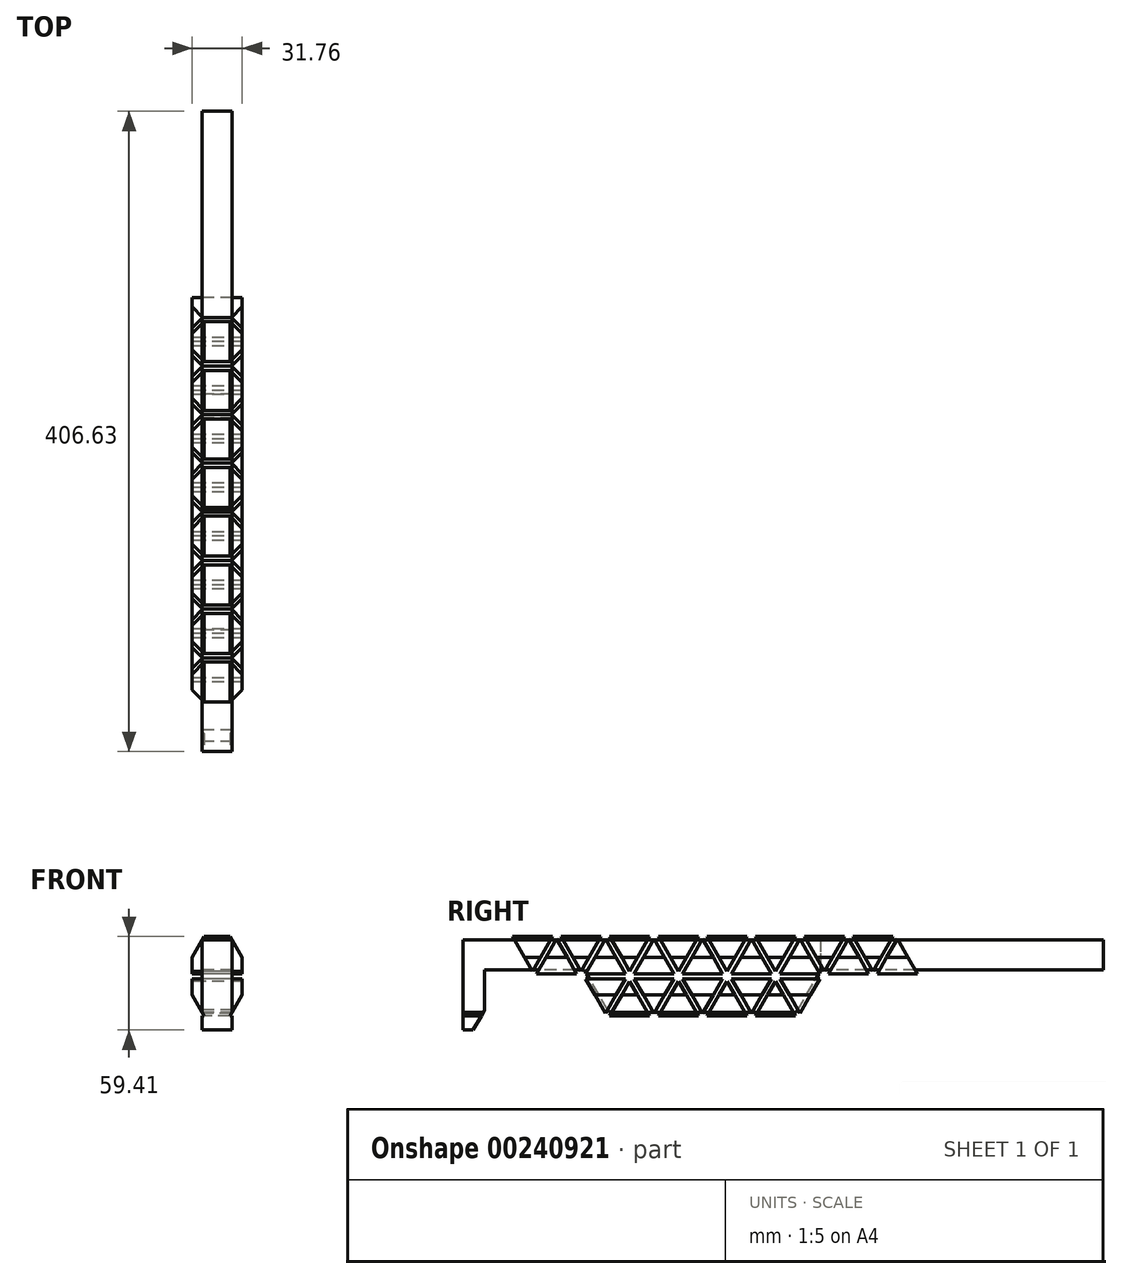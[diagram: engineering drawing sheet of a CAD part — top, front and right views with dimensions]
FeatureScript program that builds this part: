
annotation { "Feature Type Name" : "Feature", "Feature Type Description" : "" }
export const myFeature = defineFeature(function(context is Context, id is Id, definition is map)
    precondition{}
    {
        {
            var Q0;
            Q0=qCreatedBy(makeId("Right.planeOp"),FACE);
            var sketch = newSketch(context, id + "F0", { "sketchPlane" : qUnion([Q0])});
            skLineSegment(sketch, "E0", {"start": v(0, 0) * mm, "end": v(12.7, 22) * mm});
            skLineSegment(sketch, "E1", {"start": v(0, 0) * mm, "end": v(25.4, 0) * mm});
            skLineSegment(sketch, "E2", {"start": v(25.4, 0) * mm, "end": v(12.7, 22) * mm});
            skLineSegment(sketch, "E3", {"start": v(25.4, 0) * mm, "end": v(28.15, 1.59) * mm});
            skLineSegment(sketch, "E4", {"start": v(28.15, 1.59) * mm, "end": v(15.45, 23.58) * mm});
            skLineSegment(sketch, "E5", {"start": v(15.45, 23.58) * mm, "end": v(40.85, 23.58) * mm});
            skLineSegment(sketch, "E6", {"start": v(40.85, 23.58) * mm, "end": v(28.15, 1.59) * mm});
            skLineSegment(sketch, "E7", {"start": v(0, 0) * mm, "end": v(0, -3.18) * mm});
            skLineSegment(sketch, "E8", {"start": v(0, -1.59) * mm, "end": v(3.07, -1.59) * mm});
            skLineSegment(sketch, "E9.MirrorCS", {"start": v(25.4, -3.18) * mm, "end": v(12.7, -25.17) * mm});
            skLineSegment(sketch, "E10.MirrorCS", {"start": v(0, -3.18) * mm, "end": v(25.4, -3.18) * mm});
            skLineSegment(sketch, "E11.MirrorCS", {"start": v(15.45, -26.76) * mm, "end": v(40.85, -26.76) * mm});
            skLineSegment(sketch, "E12.MirrorCS", {"start": v(0, -3.17) * mm, "end": v(12.7, -25.17) * mm});
            skLineSegment(sketch, "E13.MirrorCS", {"start": v(40.85, -26.76) * mm, "end": v(28.15, -4.76) * mm});
            skLineSegment(sketch, "E14.MirrorCS", {"start": v(25.4, -3.17) * mm, "end": v(28.15, -4.76) * mm});
            skLineSegment(sketch, "E15.MirrorCS", {"start": v(28.15, -4.76) * mm, "end": v(15.45, -26.76) * mm});
            skLineSegment(sketch, "E16", {"start": v(28.15, 1.59) * mm, "end": v(28.15, -1.94) * mm});
            skLineSegment(sketch, "E17.MirrorCS", {"start": v(30.9, 0) * mm, "end": v(43.6, 22) * mm});
            skLineSegment(sketch, "E18.MirrorCS", {"start": v(56.3, 0) * mm, "end": v(30.9, 0) * mm});
            skLineSegment(sketch, "E19.MirrorCS", {"start": v(56.3, 0) * mm, "end": v(43.6, 22) * mm});
            skLineSegment(sketch, "E20.MirrorCS", {"start": v(30.9, -3.18) * mm, "end": v(43.6, -25.17) * mm});
            skLineSegment(sketch, "E21.MirrorCS", {"start": v(56.3, -3.18) * mm, "end": v(30.9, -3.18) * mm});
            skLineSegment(sketch, "E22.MirrorCS", {"start": v(56.3, -3.17) * mm, "end": v(43.6, -25.17) * mm});
            skLineSegment(sketch, "E23", {"start": v(43.6, 0) * mm, "end": v(43.6, 3.23) * mm});
            skLineSegment(sketch, "E24.MirrorCS", {"start": v(59.05, -4.76) * mm, "end": v(71.75, -26.76) * mm});
            skLineSegment(sketch, "E25.MirrorCS", {"start": v(59.05, 1.59) * mm, "end": v(71.75, 23.58) * mm});
            skLineSegment(sketch, "E26.MirrorCS", {"start": v(71.75, 23.58) * mm, "end": v(46.35, 23.58) * mm});
            skLineSegment(sketch, "E27.MirrorCS", {"start": v(46.35, 23.58) * mm, "end": v(59.05, 1.59) * mm});
            skLineSegment(sketch, "E28.MirrorCS", {"start": v(46.35, -26.76) * mm, "end": v(59.05, -4.76) * mm});
            skLineSegment(sketch, "E29.MirrorCS", {"start": v(71.75, -26.76) * mm, "end": v(46.35, -26.76) * mm});
            skLineSegment(sketch, "E30.1.0.0", {"start": v(87.2, 0) * mm, "end": v(74.5, 22) * mm});
            skLineSegment(sketch, "E30.1.0.1", {"start": v(87.2, 0) * mm, "end": v(61.8, 0) * mm});
            skLineSegment(sketch, "E30.1.0.2", {"start": v(61.8, 0) * mm, "end": v(74.5, 22) * mm});
            skLineSegment(sketch, "E30.1.0.3", {"start": v(77.25, 23.58) * mm, "end": v(89.95, 1.59) * mm});
            skLineSegment(sketch, "E30.1.0.4", {"start": v(102.65, 23.58) * mm, "end": v(77.25, 23.58) * mm});
            skLineSegment(sketch, "E30.1.0.5", {"start": v(89.95, 1.59) * mm, "end": v(102.65, 23.58) * mm});
            skLineSegment(sketch, "E30.2.0.0", {"start": v(118.1, 0) * mm, "end": v(105.4, 22) * mm});
            skLineSegment(sketch, "E30.2.0.1", {"start": v(118.1, 0) * mm, "end": v(92.7, 0) * mm});
            skLineSegment(sketch, "E30.2.0.2", {"start": v(92.7, 0) * mm, "end": v(105.4, 22) * mm});
            skLineSegment(sketch, "E30.2.0.3", {"start": v(108.15, 23.58) * mm, "end": v(120.85, 1.59) * mm});
            skLineSegment(sketch, "E30.2.0.4", {"start": v(133.55, 23.58) * mm, "end": v(108.15, 23.58) * mm});
            skLineSegment(sketch, "E30.2.0.5", {"start": v(120.85, 1.59) * mm, "end": v(133.55, 23.58) * mm});
            skLineSegment(sketch, "E30.direction1", {"start": v(56.3, 0) * mm, "end": v(87.2, 0) * mm, "construction": true});
            skLineSegment(sketch, "E31.1.0.0", {"start": v(149, 0) * mm, "end": v(136.3, 22) * mm});
            skLineSegment(sketch, "E31.1.0.1", {"start": v(123.6, 0) * mm, "end": v(136.3, 22) * mm});
            skLineSegment(sketch, "E31.1.0.2", {"start": v(149, 0) * mm, "end": v(123.6, 0) * mm});
            skLineSegment(sketch, "E31.direction1", {"start": v(118.1, 0) * mm, "end": v(149, 0) * mm, "construction": true});
            skLineSegment(sketch, "E32.MirrorCS", {"start": v(87.2, -3.17) * mm, "end": v(74.5, -25.17) * mm});
            skLineSegment(sketch, "E33.MirrorCS", {"start": v(61.8, -3.18) * mm, "end": v(74.5, -25.17) * mm});
            skLineSegment(sketch, "E34", {"start": v(87.2, -3.17) * mm, "end": v(61.8, -3.18) * mm});
            skLineSegment(sketch, "E35.1.0.0", {"start": v(-30.9, -3.18) * mm, "end": v(-5.5, -3.18) * mm});
            skLineSegment(sketch, "E35.1.0.1", {"start": v(-30.9, 0) * mm, "end": v(-5.5, 0) * mm});
            skLineSegment(sketch, "E35.1.0.2", {"start": v(-5.5, 0) * mm, "end": v(-18.2, 22) * mm});
            skLineSegment(sketch, "E35.1.0.3", {"start": v(-30.9, -3.17) * mm, "end": v(-18.2, -25.17) * mm});
            skLineSegment(sketch, "E35.1.0.4", {"start": v(-30.9, 0) * mm, "end": v(-18.2, 22) * mm});
            skLineSegment(sketch, "E35.1.0.5", {"start": v(-2.75, 1.59) * mm, "end": v(-15.45, 23.58) * mm});
            skLineSegment(sketch, "E35.1.0.6", {"start": v(-2.75, -4.76) * mm, "end": v(-15.45, -26.76) * mm});
            skLineSegment(sketch, "E35.1.0.7", {"start": v(-5.5, -3.18) * mm, "end": v(-18.2, -25.17) * mm});
            skLineSegment(sketch, "E35.1.0.8", {"start": v(9.95, -26.76) * mm, "end": v(-2.75, -4.76) * mm});
            skLineSegment(sketch, "E35.1.0.9", {"start": v(-15.45, -26.76) * mm, "end": v(9.95, -26.76) * mm});
            skLineSegment(sketch, "E35.1.0.10", {"start": v(9.95, 23.58) * mm, "end": v(-2.75, 1.59) * mm});
            skLineSegment(sketch, "E35.1.0.11", {"start": v(-15.45, 23.58) * mm, "end": v(9.95, 23.58) * mm});
            skLineSegment(sketch, "E35.2.0.0", {"start": v(-61.8, -3.18) * mm, "end": v(-36.4, -3.18) * mm});
            skLineSegment(sketch, "E35.2.0.1", {"start": v(-61.8, 0) * mm, "end": v(-36.4, 0) * mm});
            skLineSegment(sketch, "E35.2.0.2", {"start": v(-36.4, 0) * mm, "end": v(-49.1, 22) * mm});
            skLineSegment(sketch, "E35.2.0.3", {"start": v(-61.8, -3.17) * mm, "end": v(-49.1, -25.17) * mm});
            skLineSegment(sketch, "E35.2.0.4", {"start": v(-61.8, 0) * mm, "end": v(-49.1, 22) * mm});
            skLineSegment(sketch, "E35.2.0.5", {"start": v(-33.65, 1.59) * mm, "end": v(-46.35, 23.58) * mm});
            skLineSegment(sketch, "E35.2.0.6", {"start": v(-33.65, -4.76) * mm, "end": v(-46.35, -26.76) * mm});
            skLineSegment(sketch, "E35.2.0.7", {"start": v(-36.4, -3.18) * mm, "end": v(-49.1, -25.17) * mm});
            skLineSegment(sketch, "E35.2.0.8", {"start": v(-20.95, -26.76) * mm, "end": v(-33.65, -4.76) * mm});
            skLineSegment(sketch, "E35.2.0.9", {"start": v(-46.35, -26.76) * mm, "end": v(-20.95, -26.76) * mm});
            skLineSegment(sketch, "E35.2.0.10", {"start": v(-20.95, 23.58) * mm, "end": v(-33.65, 1.59) * mm});
            skLineSegment(sketch, "E35.2.0.11", {"start": v(-46.35, 23.58) * mm, "end": v(-20.95, 23.58) * mm});
            skLineSegment(sketch, "E35.direction1", {"start": v(12.7, -25.17) * mm, "end": v(-18.2, -25.17) * mm, "construction": true});
            skLineSegment(sketch, "E36.1.0.0", {"start": v(-64.55, 1.59) * mm, "end": v(-77.25, 23.58) * mm});
            skLineSegment(sketch, "E36.1.0.1", {"start": v(-51.85, 23.58) * mm, "end": v(-64.55, 1.59) * mm});
            skLineSegment(sketch, "E36.1.0.2", {"start": v(-77.25, 23.58) * mm, "end": v(-51.85, 23.58) * mm});
            skLineSegment(sketch, "E36.1.0.3", {"start": v(-67.3, 0) * mm, "end": v(-80, 22) * mm});
            skLineSegment(sketch, "E36.1.0.4", {"start": v(-92.7, 0) * mm, "end": v(-67.3, 0) * mm});
            skLineSegment(sketch, "E36.1.0.5", {"start": v(-92.7, 0) * mm, "end": v(-80, 22) * mm});
            skLineSegment(sketch, "E36.1.0.6", {"start": v(-82.75, 23.58) * mm, "end": v(-95.45, 1.59) * mm});
            skLineSegment(sketch, "E36.1.0.7", {"start": v(-108.15, 23.58) * mm, "end": v(-82.75, 23.58) * mm});
            skLineSegment(sketch, "E36.1.0.8", {"start": v(-95.45, 1.59) * mm, "end": v(-108.15, 23.58) * mm});
            skLineSegment(sketch, "E36.direction1", {"start": v(-2.75, 1.59) * mm, "end": v(-64.55, 1.59) * mm, "construction": true});
            skSolve(sketch);
        }
        {
            var Q0;
            Q0=qCreatedBy(makeId("Right.planeOp"),FACE);
            var sketch = newSketch(context, id + "F1", { "sketchPlane" : qUnion([Q0])});
            skLineSegment(sketch, "E37.0", {"start": v(-15.45, 23.58) * mm, "end": v(9.95, 23.58) * mm});
            skLineSegment(sketch, "E38.0", {"start": v(0, 0) * mm, "end": v(25.4, 0) * mm});
            skLineSegment(sketch, "E39", {"start": v(9.95, 23.58) * mm, "end": v(9.95, 0) * mm});
            skLineSegment(sketch, "E40", {"start": v(9.95, 11.8) * mm, "end": v(13.13, 11.8) * mm});
            skLineSegment(sketch, "E41", {"start": v(13.13, 11.8) * mm, "end": v(13.13, 21.32) * mm});
            skLineSegment(sketch, "E42", {"start": v(13.13, 11.8) * mm, "end": v(13.13, 2.27) * mm});
            skLineSegment(sketch, "E43", {"start": v(13.13, 21.32) * mm, "end": v(267.13, 21.32) * mm});
            skLineSegment(sketch, "E44", {"start": v(267.13, 21.32) * mm, "end": v(267.13, 2.27) * mm});
            skLineSegment(sketch, "E45", {"start": v(267.13, 2.27) * mm, "end": v(13.13, 2.27) * mm});
            skLineSegment(sketch, "E46", {"start": v(-15.45, 23.58) * mm, "end": v(-15.45, 29.93) * mm});
            skLineSegment(sketch, "E47", {"start": v(-15.45, 29.93) * mm, "end": v(9.95, 29.93) * mm});
            skLineSegment(sketch, "E48", {"start": v(9.95, 29.93) * mm, "end": v(9.95, 23.58) * mm});
            skLineSegment(sketch, "E49", {"start": v(9.95, 29.93) * mm, "end": v(-2.75, 51.93) * mm});
            skLineSegment(sketch, "E50", {"start": v(-2.75, 51.93) * mm, "end": v(-15.45, 29.93) * mm});
            skLineSegment(sketch, "E51", {"start": v(-15.45, 26.76) * mm, "end": v(-12.72, 26.76) * mm});
            skLineSegment(sketch, "E52.0", {"start": v(-5.5, 0) * mm, "end": v(-18.2, 22) * mm});
            skLineSegment(sketch, "E53.0", {"start": v(-30.9, 0) * mm, "end": v(-18.2, 22) * mm});
            skLineSegment(sketch, "E54.0", {"start": v(-30.9, 0) * mm, "end": v(-5.5, 0) * mm});
            skLineSegment(sketch, "E55.0", {"start": v(0, 0) * mm, "end": v(12.7, 22) * mm});
            skLineSegment(sketch, "E56.0", {"start": v(25.4, 0) * mm, "end": v(12.7, 22) * mm});
            skLineSegment(sketch, "E57.0.2", {"start": v(12.7, 22) * mm, "end": v(0, 0) * mm});
            skLineSegment(sketch, "E58.MirrorCS", {"start": v(-5.5, 53.52) * mm, "end": v(-18.2, 31.52) * mm});
            skLineSegment(sketch, "E59.MirrorCS", {"start": v(-30.9, 53.52) * mm, "end": v(-18.2, 31.52) * mm});
            skLineSegment(sketch, "E60.MirrorCS", {"start": v(-30.9, 53.52) * mm, "end": v(-5.5, 53.52) * mm});
            skLineSegment(sketch, "E61.MirrorCS", {"start": v(0, 53.52) * mm, "end": v(12.7, 31.52) * mm});
            skLineSegment(sketch, "E62.MirrorCS", {"start": v(25.4, 53.52) * mm, "end": v(12.7, 31.52) * mm});
            skLineSegment(sketch, "E63.MirrorCS", {"start": v(0, 53.52) * mm, "end": v(25.4, 53.52) * mm});
            skLineSegment(sketch, "E64.0", {"start": v(-36.4, -3.18) * mm, "end": v(-49.1, -25.17) * mm});
            skLineSegment(sketch, "E65", {"start": v(-42.75, -14.17) * mm, "end": v(-40, -15.76) * mm});
            skLineSegment(sketch, "E66", {"start": v(-41.37, -14.97) * mm, "end": v(-63.1, -74.64) * mm});
            skLineSegment(sketch, "E67", {"start": v(-63.1, -74.64) * mm, "end": v(-56.74, -85.64) * mm});
            skLineSegment(sketch, "E68", {"start": v(-63.1, -74.64) * mm, "end": v(-69.44, -63.64) * mm});
            skLineSegment(sketch, "E69", {"start": v(13.13, 21.32) * mm, "end": v(-139.5, 21.32) * mm});
            skLineSegment(sketch, "E70.0", {"start": v(-36.4, 0) * mm, "end": v(-49.1, 22) * mm});
            skLineSegment(sketch, "E71.0", {"start": v(-61.8, -3.17) * mm, "end": v(-49.1, -25.17) * mm});
            skPoint(sketch, "E72.0", {"position": v(12.7, -3.18) * mm});
            skLineSegment(sketch, "E73.0", {"start": v(46.35, -26.76) * mm, "end": v(59.05, -4.76) * mm});
            skLineSegment(sketch, "E74.0", {"start": v(87.2, -3.17) * mm, "end": v(74.5, -25.17) * mm});
            skLineSegment(sketch, "E75", {"start": v(72.27, -24.5) * mm, "end": v(-46.87, -24.5) * mm});
            skLineSegment(sketch, "E76", {"start": v(72.27, -24.5) * mm, "end": v(87.72, 2.27) * mm});
            skLineSegment(sketch, "E77", {"start": v(87.72, 2.27) * mm, "end": v(87.72, 21.32) * mm});
            skLineSegment(sketch, "E78", {"start": v(13.13, 2.27) * mm, "end": v(-125.82, 2.27) * mm});
            skLineSegment(sketch, "E79", {"start": v(-46.87, -24.5) * mm, "end": v(-62.32, 2.27) * mm});
            skLineSegment(sketch, "E80", {"start": v(-69.44, -63.64) * mm, "end": v(-51.98, -15.65) * mm});
            skLineSegment(sketch, "E81", {"start": v(-56.74, -85.64) * mm, "end": v(-34.49, -24.5) * mm});
            skLineSegment(sketch, "E82", {"start": v(-125.82, 2.27) * mm, "end": v(-125.82, -23.13) * mm});
            skLineSegment(sketch, "E83", {"start": v(-125.82, -23.13) * mm, "end": v(-133.15, -35.83) * mm});
            skLineSegment(sketch, "E84", {"start": v(-133.15, -35.83) * mm, "end": v(-139.5, -35.83) * mm});
            skLineSegment(sketch, "E85", {"start": v(-139.5, -35.83) * mm, "end": v(-139.5, 21.32) * mm});
            skSolve(sketch);
        }
        {
            var Q0;
            {var subQ0=sQuery(id+"F1.wireOp",EDGE,"E82");Q0=makeQuery(id+"F1.imprint","IMPRINT",FACE,{"disambiguationData":[TD([[makeQuery(id+"F1.imprint","IMPRINT",EDGE,{"derivedFrom":subQ0}),-1.0]])]});}
            var Q1;
            {var subQ0=sQuery(id+"F1.wireOp",EDGE,"E69");var subQ1=sQuery(id+"F1.wireOp",EDGE,"E53.0");var subQ2=makeQuery(id+"F1.imprint","INTERSECT",VERTEX,{"derivedFrom":[subQ1,subQ0]});Q1=makeQuery(id+"F1.imprint","IMPRINT",FACE,{"disambiguationData":[TD([[makeQuery(id+"F1.imprint","IMPRINT",EDGE,{"disambiguationData":[TD([[subQ2,1.0]])],"derivedFrom":subQ1}),1.0]])]});}
            var Q2;
            {var subQ0=sQuery(id+"F1.wireOp",EDGE,"E69");var subQ1=sQuery(id+"F1.wireOp",EDGE,"E52.0");var subQ2=makeQuery(id+"F1.imprint","INTERSECT",VERTEX,{"derivedFrom":[subQ1,subQ0]});Q2=makeQuery(id+"F1.imprint","IMPRINT",FACE,{"disambiguationData":[TD([[makeQuery(id+"F1.imprint","IMPRINT",EDGE,{"disambiguationData":[TD([[subQ2,1.0]])],"derivedFrom":subQ1}),1.0]])]});}
            var Q3;
            {var subQ0=sQuery(id+"F1.wireOp",EDGE,"E69");var subQ1=sQuery(id+"F1.wireOp",EDGE,"E39");var subQ2=makeQuery(id+"F1.imprint","INTERSECT",VERTEX,{"derivedFrom":[subQ1,subQ0]});Q3=makeQuery(id+"F1.imprint","IMPRINT",FACE,{"disambiguationData":[TD([[makeQuery(id+"F1.imprint","IMPRINT",EDGE,{"disambiguationData":[TD([[subQ2,-1.0]])],"derivedFrom":subQ1}),-1.0]])]});}
            var Q4;
            {var subQ0=sQuery(id+"F1.wireOp",EDGE,"E42");Q4=makeQuery(id+"F1.imprint","IMPRINT",FACE,{"disambiguationData":[TD([[makeQuery(id+"F1.imprint","IMPRINT",EDGE,{"derivedFrom":subQ0}),1.0]])]});}
            var Q5;
            {var subQ0=sQuery(id+"F1.wireOp",EDGE,"E40");Q5=makeQuery(id+"F1.imprint","IMPRINT",FACE,{"disambiguationData":[TD([[makeQuery(id+"F1.imprint","IMPRINT",EDGE,{"derivedFrom":subQ0}),-1.0]])]});}
            var Q6;
            {var subQ1=sQuery(id+"F1.wireOp",EDGE,"E40");Q6=makeQuery(id+"F1.imprint","IMPRINT",FACE,{"disambiguationData":[TD([[makeQuery(id+"F1.imprint","IMPRINT",EDGE,{"derivedFrom":subQ1}),1.0]])]});}
            var Q7;
            {var subQ0=sQuery(id+"F1.wireOp",EDGE,"E39");var subQ1=makeQuery(id+"F1.imprint","INTERSECT",VERTEX,{"derivedFrom":[subQ0,sQuery(id+"F1.wireOp",EDGE,"E40")]});Q7=makeQuery(id+"F1.imprint","IMPRINT",FACE,{"disambiguationData":[TD([[makeQuery(id+"F1.imprint","IMPRINT",EDGE,{"disambiguationData":[TD([[subQ1,1.0]])],"derivedFrom":subQ0}),-1.0]])]});}
            var Q8;
            {var subQ0=sQuery(id+"F1.wireOp",EDGE,"E69");var subQ1=sQuery(id+"F1.wireOp",EDGE,"E39");var subQ2=makeQuery(id+"F1.imprint","INTERSECT",VERTEX,{"derivedFrom":[subQ1,subQ0]});Q8=makeQuery(id+"F1.imprint","IMPRINT",FACE,{"disambiguationData":[TD([[makeQuery(id+"F1.imprint","IMPRINT",EDGE,{"disambiguationData":[TD([[subQ2,-1.0]])],"derivedFrom":subQ1}),1.0]])]});}
            var Q9;
            {var subQ7=sQuery(id+"F1.wireOp",EDGE,"E77");Q9=makeQuery(id+"F1.imprint","IMPRINT",FACE,{"disambiguationData":[TD([[makeQuery(id+"F1.imprint","IMPRINT",EDGE,{"derivedFrom":subQ7}),1.0]])]});}
            var Q10;
            {var subQ20=sQuery(id+"F1.wireOp",EDGE,"E54.0");Q10=makeQuery(id+"F1.imprint","IMPRINT",FACE,{"disambiguationData":[TD([[makeQuery(id+"F1.imprint","IMPRINT",EDGE,{"derivedFrom":subQ20}),-1.0]])]});}
            var Q11;
            {var subQ0=sQuery(id+"F1.wireOp",EDGE,"E38.0");var subQ1=sQuery(id+"F1.wireOp",EDGE,"E39");var subQ2=makeQuery(id+"F1.imprint","INTERSECT",VERTEX,{"derivedFrom":[subQ1,subQ0]});Q11=makeQuery(id+"F1.imprint","IMPRINT",FACE,{"disambiguationData":[TD([[makeQuery(id+"F1.imprint","IMPRINT",EDGE,{"disambiguationData":[TD([[subQ2,1.0]])],"derivedFrom":subQ1}),1.0]])]});}
            var Q12;
            {var subQ0=sQuery(id+"F1.wireOp",EDGE,"E38.0");var subQ1=sQuery(id+"F1.wireOp",EDGE,"E39");var subQ2=makeQuery(id+"F1.imprint","INTERSECT",VERTEX,{"derivedFrom":[subQ1,subQ0]});Q12=makeQuery(id+"F1.imprint","IMPRINT",FACE,{"disambiguationData":[TD([[makeQuery(id+"F1.imprint","IMPRINT",EDGE,{"disambiguationData":[TD([[subQ2,1.0]])],"derivedFrom":subQ1}),-1.0]])]});}
            var Q13;
            {var subQ0=sQuery(id+"F1.wireOp",EDGE,"E54.0");Q13=makeQuery(id+"F1.imprint","IMPRINT",FACE,{"disambiguationData":[TD([[makeQuery(id+"F1.imprint","IMPRINT",EDGE,{"derivedFrom":subQ0}),1.0]])]});}
            var Q14;
            {var subQ1=sQuery(id+"F1.wireOp",EDGE,"E65");var subQ5=sQuery(id+"F1.wireOp",EDGE,"E64.0");var subQ6=makeQuery(id+"F1.imprint","INTERSECT",VERTEX,{"derivedFrom":[subQ5,subQ1]});Q14=makeQuery(id+"F1.imprint","IMPRINT",FACE,{"disambiguationData":[TD([[makeQuery(id+"F1.imprint","IMPRINT",EDGE,{"disambiguationData":[TD([[subQ6,-1.0]])],"derivedFrom":subQ5}),1.0]])]});}
            extrude(context, id + "F2", {"entities" : qUnion([Q0, Q1, Q2, Q3, Q4, Q5, Q6, Q7, Q8, Q9, Q10, Q11, Q12, Q13, Q14]), "endBound" : BoundingType.SYMMETRIC, "depth" : 19.05 * mm});
        }
        {
            var Q0;
            {var subQ0=sQuery(id+"F1.wireOp",EDGE,"E44");Q0=makeQuery(id+"F1.imprint","IMPRINT",FACE,{"disambiguationData":[TD([[makeQuery(id+"F1.imprint","IMPRINT",EDGE,{"derivedFrom":subQ0}),-1.0]])]});}
            extrude(context, id + "F3", {"entities" : qUnion([Q0]), "endBound" : BoundingType.SYMMETRIC, "depth" : 19.05 * mm});
        }
        {
            var Q0;
            Q0=makeQuery(id+"F0.imprint","IMPRINT",FACE,{"disambiguationData":[TD([[makeQuery(id+"F0.imprint","IMPRINT",EDGE,{"derivedFrom":sQuery(id+"F0.wireOp",EDGE,"E30.1.0.3")}),1.0]])]});
            var Q1;
            Q1=makeQuery(id+"F0.imprint","IMPRINT",FACE,{"disambiguationData":[TD([[makeQuery(id+"F0.imprint","IMPRINT",EDGE,{"derivedFrom":sQuery(id+"F0.wireOp",EDGE,"E30.1.0.0")}),1.0]])]});
            var Q2;
            Q2=makeQuery(id+"F0.imprint","IMPRINT",FACE,{"disambiguationData":[TD([[makeQuery(id+"F0.imprint","IMPRINT",EDGE,{"derivedFrom":sQuery(id+"F0.wireOp",EDGE,"E32.MirrorCS")}),-1.0]])]});
            var Q3;
            Q3=makeQuery(id+"F0.imprint","IMPRINT",FACE,{"disambiguationData":[TD([[makeQuery(id+"F0.imprint","IMPRINT",EDGE,{"derivedFrom":sQuery(id+"F0.wireOp",EDGE,"E24.MirrorCS")}),-1.0]])]});
            var Q4;
            Q4=makeQuery(id+"F0.imprint","IMPRINT",FACE,{"disambiguationData":[TD([[makeQuery(id+"F0.imprint","IMPRINT",EDGE,{"derivedFrom":sQuery(id+"F0.wireOp",EDGE,"E20.MirrorCS")}),1.0]])]});
            var Q5;
            Q5=makeQuery(id+"F0.imprint","IMPRINT",FACE,{"disambiguationData":[TD([[makeQuery(id+"F0.imprint","IMPRINT",EDGE,{"derivedFrom":sQuery(id+"F0.wireOp",EDGE,"E25.MirrorCS")}),1.0]])]});
            var Q6;
            {var subQ0=sQuery(id+"F0.wireOp",EDGE,"E17.MirrorCS");Q6=makeQuery(id+"F0.imprint","IMPRINT",FACE,{"disambiguationData":[TD([[makeQuery(id+"F0.imprint","IMPRINT",EDGE,{"derivedFrom":subQ0}),-1.0]])]});}
            var Q7;
            Q7=makeQuery(id+"F0.imprint","IMPRINT",FACE,{"disambiguationData":[TD([[makeQuery(id+"F0.imprint","IMPRINT",EDGE,{"derivedFrom":sQuery(id+"F0.wireOp",EDGE,"E11.MirrorCS")}),1.0]])]});
            var Q8;
            Q8=makeQuery(id+"F0.imprint","IMPRINT",FACE,{"disambiguationData":[TD([[makeQuery(id+"F0.imprint","IMPRINT",EDGE,{"derivedFrom":sQuery(id+"F0.wireOp",EDGE,"E4")}),-1.0]])]});
            var Q9;
            Q9=makeQuery(id+"F0.imprint","IMPRINT",FACE,{"disambiguationData":[TD([[makeQuery(id+"F0.imprint","IMPRINT",EDGE,{"derivedFrom":sQuery(id+"F0.wireOp",EDGE,"E0")}),-1.0]])]});
            var Q10;
            Q10=makeQuery(id+"F0.imprint","IMPRINT",FACE,{"disambiguationData":[TD([[makeQuery(id+"F0.imprint","IMPRINT",EDGE,{"derivedFrom":sQuery(id+"F0.wireOp",EDGE,"E9.MirrorCS")}),-1.0]])]});
            var Q11;
            Q11=makeQuery(id+"F0.imprint","IMPRINT",FACE,{"disambiguationData":[TD([[makeQuery(id+"F0.imprint","IMPRINT",EDGE,{"derivedFrom":sQuery(id+"F0.wireOp",EDGE,"E35.1.0.6")}),1.0]])]});
            var Q12;
            Q12=makeQuery(id+"F0.imprint","IMPRINT",FACE,{"disambiguationData":[TD([[makeQuery(id+"F0.imprint","IMPRINT",EDGE,{"derivedFrom":sQuery(id+"F0.wireOp",EDGE,"E35.1.0.5")}),-1.0]])]});
            var Q13;
            Q13=makeQuery(id+"F0.imprint","IMPRINT",FACE,{"disambiguationData":[TD([[makeQuery(id+"F0.imprint","IMPRINT",EDGE,{"derivedFrom":sQuery(id+"F0.wireOp",EDGE,"E35.1.0.1")}),1.0]])]});
            var Q14;
            Q14=makeQuery(id+"F0.imprint","IMPRINT",FACE,{"disambiguationData":[TD([[makeQuery(id+"F0.imprint","IMPRINT",EDGE,{"derivedFrom":sQuery(id+"F0.wireOp",EDGE,"E35.1.0.0")}),-1.0]])]});
            var Q15;
            Q15=makeQuery(id+"F0.imprint","IMPRINT",FACE,{"disambiguationData":[TD([[makeQuery(id+"F0.imprint","IMPRINT",EDGE,{"derivedFrom":sQuery(id+"F0.wireOp",EDGE,"E35.2.0.6")}),1.0]])]});
            var Q16;
            Q16=makeQuery(id+"F0.imprint","IMPRINT",FACE,{"disambiguationData":[TD([[makeQuery(id+"F0.imprint","IMPRINT",EDGE,{"derivedFrom":sQuery(id+"F0.wireOp",EDGE,"E35.2.0.5")}),-1.0]])]});
            var Q17;
            Q17=makeQuery(id+"F0.imprint","IMPRINT",FACE,{"disambiguationData":[TD([[makeQuery(id+"F0.imprint","IMPRINT",EDGE,{"derivedFrom":sQuery(id+"F0.wireOp",EDGE,"E35.2.0.1")}),1.0]])]});
            var Q18;
            Q18=makeQuery(id+"F0.imprint","IMPRINT",FACE,{"disambiguationData":[TD([[makeQuery(id+"F0.imprint","IMPRINT",EDGE,{"derivedFrom":sQuery(id+"F0.wireOp",EDGE,"E35.2.0.0")}),-1.0]])]});
            var Q19;
            Q19=makeQuery(id+"F0.imprint","IMPRINT",FACE,{"disambiguationData":[TD([[makeQuery(id+"F0.imprint","IMPRINT",EDGE,{"derivedFrom":sQuery(id+"F0.wireOp",EDGE,"E36.1.0.0")}),-1.0]])]});
            var Q20;
            Q20=makeQuery(id+"F0.imprint","IMPRINT",FACE,{"disambiguationData":[TD([[makeQuery(id+"F0.imprint","IMPRINT",EDGE,{"derivedFrom":sQuery(id+"F0.wireOp",EDGE,"E36.1.0.3")}),1.0]])]});
            var Q21;
            Q21=makeQuery(id+"F0.imprint","IMPRINT",FACE,{"disambiguationData":[TD([[makeQuery(id+"F0.imprint","IMPRINT",EDGE,{"derivedFrom":sQuery(id+"F0.wireOp",EDGE,"E36.1.0.6")}),-1.0]])]});
            var Q22;
            Q22=makeQuery(id+"F0.imprint","IMPRINT",FACE,{"disambiguationData":[TD([[makeQuery(id+"F0.imprint","IMPRINT",EDGE,{"derivedFrom":sQuery(id+"F0.wireOp",EDGE,"E30.2.0.0")}),1.0]])]});
            var Q23;
            Q23=makeQuery(id+"F0.imprint","IMPRINT",FACE,{"disambiguationData":[TD([[makeQuery(id+"F0.imprint","IMPRINT",EDGE,{"derivedFrom":sQuery(id+"F0.wireOp",EDGE,"E30.2.0.3")}),1.0]])]});
            var Q24;
            Q24=makeQuery(id+"F0.imprint","IMPRINT",FACE,{"disambiguationData":[TD([[makeQuery(id+"F0.imprint","IMPRINT",EDGE,{"derivedFrom":sQuery(id+"F0.wireOp",EDGE,"E31.1.0.0")}),1.0]])]});
            extrude(context, id + "F4", {"entities" : qUnion([Q0, Q1, Q2, Q3, Q4, Q5, Q6, Q7, Q8, Q9, Q10, Q11, Q12, Q13, Q14, Q15, Q16, Q17, Q18, Q19, Q20, Q21, Q22, Q23, Q24]), "endBound" : BoundingType.SYMMETRIC, "depth" : 31.75 * mm});
        }
        {
            var Q0;
            Q0=qCreatedBy(makeId("Front.planeOp"),FACE);
            var sketch = newSketch(context, id + "F5", { "sketchPlane" : qUnion([Q0])});
            skLineSegment(sketch, "E86.0", {"start": v(15.88, 23.58) * mm, "end": v(-15.88, 23.58) * mm});
            skLineSegment(sketch, "E87.0", {"start": v(15.88, -26.76) * mm, "end": v(-15.88, -26.76) * mm});
            skPoint(sketch, "E88.0", {"position": v(9.53, 21.32) * mm});
            skPoint(sketch, "E89.0", {"position": v(-9.53, 21.32) * mm});
            skPoint(sketch, "E90.0", {"position": v(-9.53, -24.5) * mm});
            skPoint(sketch, "E91.0", {"position": v(9.53, -24.5) * mm});
            skLineSegment(sketch, "E92", {"start": v(8.22, -26.76) * mm, "end": v(9.53, -24.5) * mm});
            skLineSegment(sketch, "E93.0", {"start": v(15.88, -4.76) * mm, "end": v(15.88, -26.76) * mm});
            skLineSegment(sketch, "E94.0", {"start": v(-15.88, -4.76) * mm, "end": v(-15.88, -26.76) * mm});
            skLineSegment(sketch, "E95.0", {"start": v(-15.88, 1.59) * mm, "end": v(-15.88, 23.58) * mm});
            skLineSegment(sketch, "E96.0", {"start": v(15.88, 1.59) * mm, "end": v(15.88, 23.58) * mm});
            skLineSegment(sketch, "E97", {"start": v(9.53, -24.5) * mm, "end": v(15.88, -13.5) * mm});
            skLineSegment(sketch, "E98", {"start": v(0, -26.76) * mm, "end": v(0, -24.74) * mm});
            skPoint(sketch, "E98.endSnap0", {"position": v(0, -26.76) * mm});
            skLineSegment(sketch, "E99.MirrorCS", {"start": v(-8.22, -26.76) * mm, "end": v(-9.53, -24.5) * mm});
            skLineSegment(sketch, "E100.MirrorCS", {"start": v(-9.52, -24.5) * mm, "end": v(-15.88, -13.5) * mm});
            skLineSegment(sketch, "E101", {"start": v(-9.53, 21.32) * mm, "end": v(-8.22, 23.58) * mm});
            skLineSegment(sketch, "E102.0.0", {"start": v(-15.88, 23.58) * mm, "end": v(-15.88, 1.59) * mm});
            skLineSegment(sketch, "E102.0.1", {"start": v(-15.88, 1.59) * mm, "end": v(15.88, 1.59) * mm});
            skLineSegment(sketch, "E103", {"start": v(-9.53, 21.32) * mm, "end": v(-15.88, 10.32) * mm});
            skLineSegment(sketch, "E104", {"start": v(0, 23.58) * mm, "end": v(0, 22.73) * mm});
            skPoint(sketch, "E104.endSnap0", {"position": v(0, 23.58) * mm});
            skLineSegment(sketch, "E105.MirrorCS", {"start": v(9.53, 21.32) * mm, "end": v(8.22, 23.58) * mm});
            skLineSegment(sketch, "E106.MirrorCS", {"start": v(9.53, 21.32) * mm, "end": v(15.88, 10.32) * mm});
            skSolve(sketch);
        }
        {
            var Q0;
            {var subQ3=sQuery(id+"F5.wireOp",EDGE,"E92");Q0=makeQuery(id+"F5.imprint","IMPRINT",FACE,{"disambiguationData":[TD([[makeQuery(id+"F5.imprint","IMPRINT",EDGE,{"derivedFrom":subQ3}),-1.0]])]});}
            var Q1;
            {var subQ3=sQuery(id+"F5.wireOp",EDGE,"E99.MirrorCS");Q1=makeQuery(id+"F5.imprint","IMPRINT",FACE,{"disambiguationData":[TD([[makeQuery(id+"F5.imprint","IMPRINT",EDGE,{"derivedFrom":subQ3}),1.0]])]});}
            var Q2;
            {var subQ0=sQuery(id+"F5.wireOp",EDGE,"E101");Q2=makeQuery(id+"F5.imprint","IMPRINT",FACE,{"disambiguationData":[TD([[makeQuery(id+"F5.imprint","IMPRINT",EDGE,{"derivedFrom":subQ0}),1.0]])]});}
            var Q3;
            {var subQ4=sQuery(id+"F5.wireOp",EDGE,"E105.MirrorCS");Q3=makeQuery(id+"F5.imprint","IMPRINT",FACE,{"disambiguationData":[TD([[makeQuery(id+"F5.imprint","IMPRINT",EDGE,{"derivedFrom":subQ4}),-1.0]])]});}
            extrude(context, id + "F6", {"entities" : qUnion([Q0, Q1, Q2, Q3]), "operationType" : NewBodyOperationType.REMOVE, "endBound" : BoundingType.SYMMETRIC, "oppositeDirection" : true, "depth" : 355.6 * mm});
        }
    });
